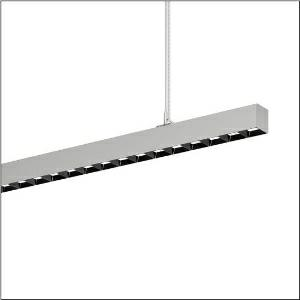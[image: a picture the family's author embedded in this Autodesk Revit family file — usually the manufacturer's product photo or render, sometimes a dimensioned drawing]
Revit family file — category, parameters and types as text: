
# Revit family: silica_21_51mx34dc4dsb
name_source: partatom
category: Lighting Fixtures
units: mm (PartAtom-declared; Revit-internal decimal feet)

## family parameters
Cut with Voids When Loaded = No
Host = Face
Light Source = No
Part Type = Normal
Room Calculation Point = No
Round Connector Dimension = Use Diameter
Shared = No

## types (1)
- --- (1 x LED, 19200 lm, 120.3 W, 4000K)
    Apparent Load = 120 VA
    CIE Flux Codes = 74 94 99 56 100
    Color Rendering = 80
    Color Temperature = 4000K
    Default Elevation = 1800 mm
    Description = Silica 21, office luminaire, primary light control with darklight reflector, of PMMA, black, light emission: direct/indirect distribution, primary light characteristic: asymmetric, installation type: suspended mounting, LED, rated luminous flux: 19.200lm, luminous efficacy: 160lm/W, light colour: 840, colour temperature: 4000K, control gear: DALI 2, with terminal, 3+2-pole, max. 2.5mm², mains connection: 220..240V, AC, 50/60Hz, rated input power: 120.3W, luminaire housing, of aluminium, metallic grey (RAL 9006), length: 3.004mm, width: 53mm, height: 53mm, protection rating (complete): IP20, insulation class (complete): insulation class I (protective earthing), certification: CE, permissible operating ambient temperature: 0..+35°C, standard: EN 50419, packaging unit: 1 piece
    Height = 53 mm
    Lamp = 1 x LED
    Lamp Light Flux = 19200 lm
    Lamp Power = 120.3 W
    Lamp count = 1
    Length = 3004 mm
    Luminous efficacy = 160 lm/W
    Manufacturer = Siteco
    ModVariant = No
    Model = 51MX34DC4DSB
    Mounting Place = Ceiling
    Mounting Type = Pendant
    Number of Poles = 1
    OnlyDefault = Yes
    Power Factor = 1
    Product Name = Silica 21
    Product group = office luminaire | ceiling pendant
    ProductGroupID = 903
    Protection Class = Protection class I
    Protection Degree = IP 20
    RLX_Detail_Level = 1
    RLX_Emergency_Light_Flux = 0 lm
    RLX_Emergency_Type = 0
    RLX_Emergency_Type_DB = No
    RlxData = <blob elided: 66289 chars, md5=d96fe1a5>
    Socket = socket
    Standby Power = 0 W
    System Light Flux = 19200 lm
    System Power = 120 W
    Type Comments = factory setting: luminous flux: 100 % | dim-lin: 254 | 418 mA
    Type Image = l_1335859.jpg
    URL = http://relux.com
    VarID = @adj_120051
    Voltage = 0 V
    Weight = 0.00 kg
    Width = 53 mm

## geometry (parser evidence)
native form markers: Blend x4, Sweep x12
no freeform markers — native parametric forms only
